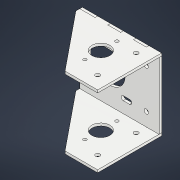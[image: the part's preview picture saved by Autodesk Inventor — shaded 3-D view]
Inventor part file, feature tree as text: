
AUTODESK INVENTOR PART (.ipt)
format: ipt  version: 2022 (Build 260153000, 153)  size: 163,328 bytes
history: imported  units: in
note: dims shown in document units (in); Inventor stores cm internally (conversion verified against a paired STEP export)
features: imported_body x1
ambient origin geometry x8: Origin, YZ Plane, XZ Plane, XY Plane, X Axis, Y Axis, Z Axis, Center Point
bodies: Solid1 (imported_parasolid), Solid2 (imported_parasolid), Solid3 (imported_parasolid), Body3 (imported_parasolid), Body4 (imported_parasolid), Body5 (imported_parasolid)
feature tree (1):
  imported_body  NMx_Import_Brep_tag  [imported B-rep: ~92 faces, bbox_mm=[62.0, 56.064, 50.0]]
